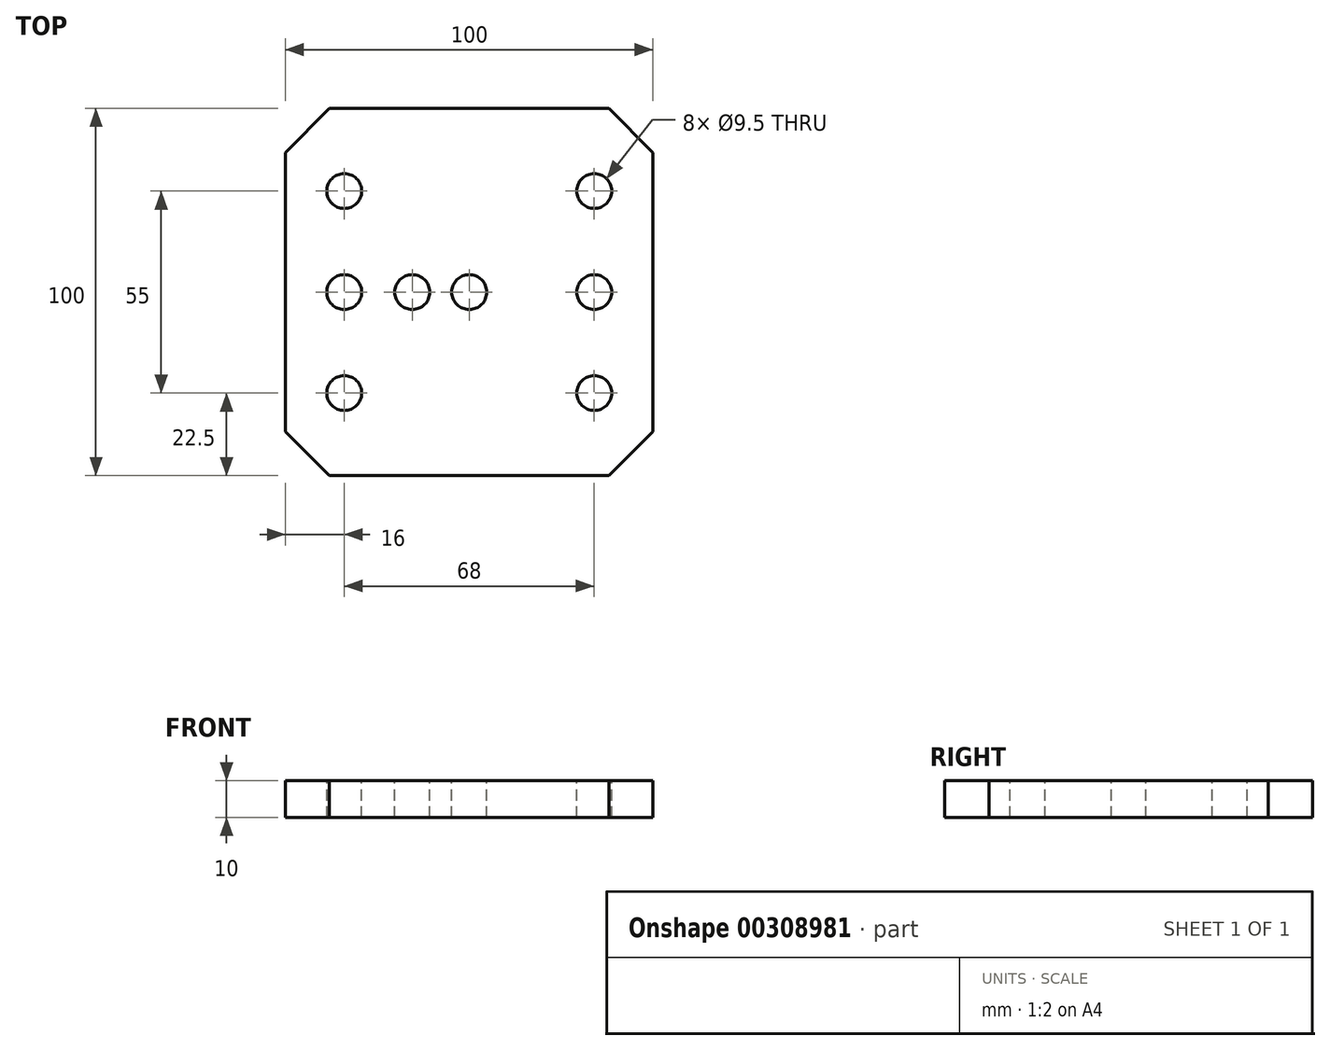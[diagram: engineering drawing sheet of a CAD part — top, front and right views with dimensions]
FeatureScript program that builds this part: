
annotation { "Feature Type Name" : "Feature", "Feature Type Description" : "" }
export const myFeature = defineFeature(function(context is Context, id is Id, definition is map)
    precondition{}
    {
        {
            var Q0;
            Q0=qCreatedBy(makeId("Top.planeOp"),FACE);
            var sketch = newSketch(context, id + "F0", { "sketchPlane" : qUnion([Q0])});
            skLineSegment(sketch, "E0.bottom", {"start": v(50, 50) * mm, "end": v(-50, 50) * mm});
            skLineSegment(sketch, "E0.top", {"start": v(50, -50) * mm, "end": v(-50, -50) * mm});
            skLineSegment(sketch, "E0.left", {"start": v(50, 50) * mm, "end": v(50, -50) * mm});
            skLineSegment(sketch, "E0.right", {"start": v(-50, 50) * mm, "end": v(-50, -50) * mm});
            skPoint(sketch, "E0.middle", {"position": v(0, 0) * mm});
            skSolve(sketch);
        }
        {
            var Q0;
            Q0=makeQuery(id+"F0.imprint","IMPRINT",FACE,{"disambiguationData":[TD([[makeQuery(id+"F0.imprint","IMPRINT",EDGE,{"derivedFrom":sQuery(id+"F0.wireOp",EDGE,"E0.bottom")}),1.0]])]});
            extrude(context, id + "F1", {"entities" : qUnion([Q0]), "depth" : 10 * mm});
        }
        {
            var Q0;
            Q0=makeQuery(id+"F1.opExtrude","SWEPT_EDGE",EDGE,{"disambiguationData":[OSD([sQuery(id+"F0.wireOp",EDGE,"E0.top"),sQuery(id+"F0.wireOp",EDGE,"E0.left")])]});
            var Q1;
            Q1=makeQuery(id+"F1.opExtrude","SWEPT_EDGE",EDGE,{"disambiguationData":[OSD([sQuery(id+"F0.wireOp",EDGE,"E0.bottom"),sQuery(id+"F0.wireOp",EDGE,"E0.left")])]});
            var Q2;
            Q2=makeQuery(id+"F1.opExtrude","SWEPT_EDGE",EDGE,{"disambiguationData":[OSD([sQuery(id+"F0.wireOp",EDGE,"E0.top"),sQuery(id+"F0.wireOp",EDGE,"E0.right")])]});
            var Q3;
            Q3=makeQuery(id+"F1.opExtrude","SWEPT_EDGE",EDGE,{"disambiguationData":[OSD([sQuery(id+"F0.wireOp",EDGE,"E0.bottom"),sQuery(id+"F0.wireOp",EDGE,"E0.right")])]});
            chamfer(context, id + "F2", {"entities" : qUnion([Q0, Q1, Q2, Q3]), "width" : 12 * mm, "tangentPropagation" : true});
        }
        {
            var Q0;
            Q0=makeQuery(id+"F1.opExtrude","CAP_FACE",FACE,{"disambiguationData":[OSD([sQuery(id+"F0.wireOp",EDGE,"E0.bottom"),sQuery(id+"F0.wireOp",EDGE,"E0.top"),sQuery(id+"F0.wireOp",EDGE,"E0.left"),sQuery(id+"F0.wireOp",EDGE,"E0.right")])],"isStart":false});
            var sketch = newSketch(context, id + "F3", { "sketchPlane" : qUnion([Q0])});
            skLineSegment(sketch, "E1", {"start": v(-34, 33.97) * mm, "end": v(-34, -36.88) * mm, "construction": true});
            skLineSegment(sketch, "E2", {"start": v(0, 0) * mm, "end": v(34, 0) * mm, "construction": true});
            skPoint(sketch, "E2.endSnap0", {"position": v(50, 0) * mm});
            skPoint(sketch, "E3", {"position": v(-34, 27.5) * mm});
            skPoint(sketch, "E4", {"position": v(-34, 0) * mm});
            skPoint(sketch, "E5", {"position": v(-34, -27.5) * mm});
            skPoint(sketch, "E6", {"position": v(-15.5, 0) * mm});
            skPoint(sketch, "E7", {"position": v(34, 0) * mm});
            skPoint(sketch, "E8", {"position": v(34, 27.5) * mm});
            skPoint(sketch, "E9", {"position": v(34, -27.5) * mm});
            skPoint(sketch, "E10", {"position": v(0, 0) * mm});
            skSolve(sketch);
        }
        {
            var Q0;
            Q0=sQuery(id+"F3.wireOp",VERTEX,"E6");
            var Q1;
            Q1=sQuery(id+"F3.wireOp",VERTEX,"E4");
            var Q2;
            Q2=sQuery(id+"F3.wireOp",VERTEX,"E5");
            var Q3;
            Q3=sQuery(id+"F3.wireOp",VERTEX,"E3");
            var Q4;
            Q4=sQuery(id+"F3.wireOp",VERTEX,"E8");
            var Q5;
            Q5=sQuery(id+"F3.wireOp",VERTEX,"E7");
            var Q6;
            Q6=sQuery(id+"F3.wireOp",VERTEX,"E9");
            var Q7;
            Q7=sQuery(id+"F3.wireOp",VERTEX,"E10");
            var Q8;
            Q8=makeQuery(id+"F1.opExtrude","SWEPT_BODY",BODY,{"disambiguationData":[OSD([sQuery(id+"F0.wireOp",EDGE,"E0.bottom"),sQuery(id+"F0.wireOp",EDGE,"E0.top"),sQuery(id+"F0.wireOp",EDGE,"E0.left"),sQuery(id+"F0.wireOp",EDGE,"E0.right")])]});
            hole(context, id + "F4", {"style" : HoleStyle.SIMPLE, "endStyle" : HoleEndStyle.THROUGH, "holeDiameter" : 9.5 * mm, "tappedDepth" : 12 * mm, "tapClearance" : 3, "locations" : qUnion([Q0, Q1, Q2, Q3, Q4, Q5, Q6, Q7]), "scope" : qUnion([Q8])});
        }
    });
